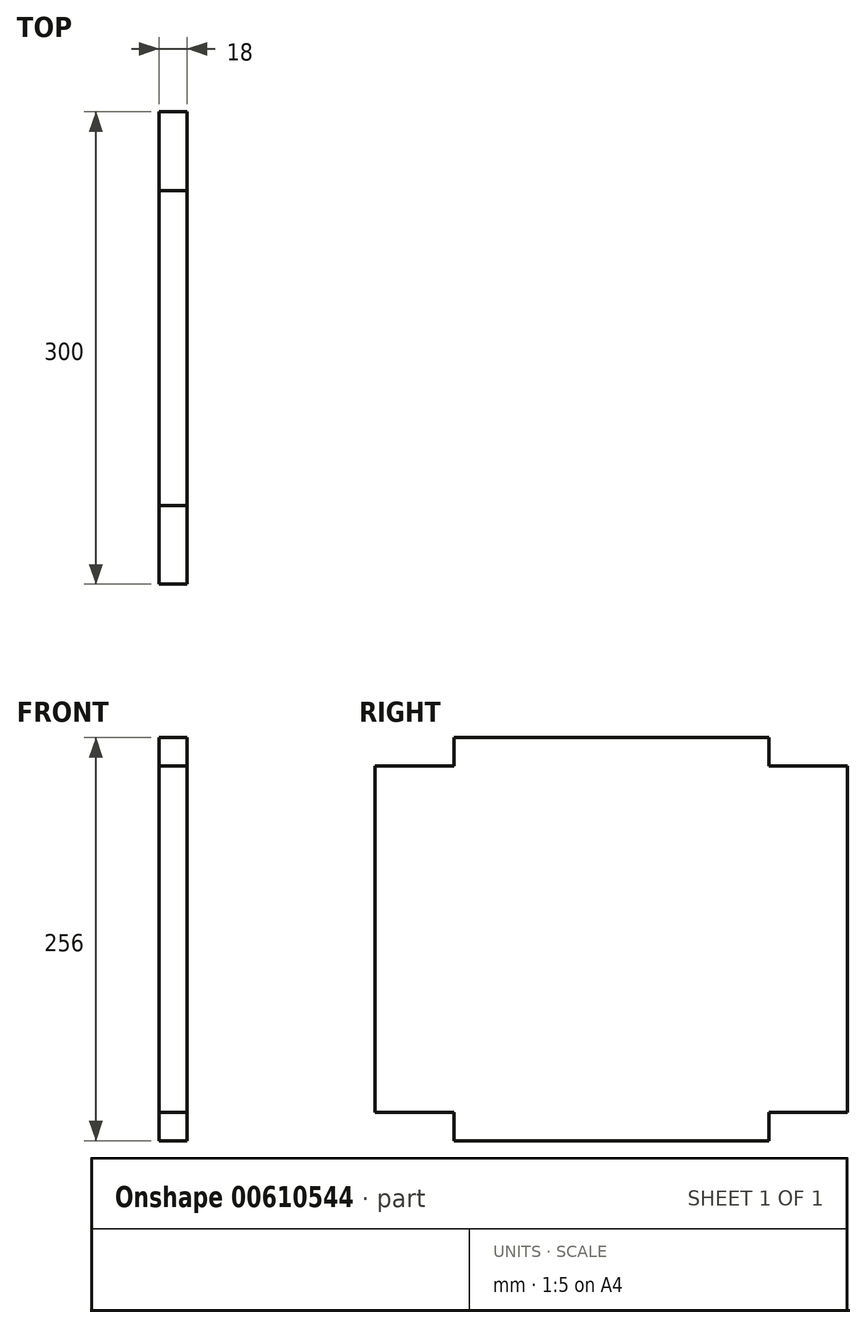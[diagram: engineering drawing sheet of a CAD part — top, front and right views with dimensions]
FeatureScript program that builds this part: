
annotation { "Feature Type Name" : "Feature", "Feature Type Description" : "" }
export const myFeature = defineFeature(function(context is Context, id is Id, definition is map)
    precondition{}
    {
        {
            var Q0;
            Q0=qCreatedBy(makeId("Right.planeOp"),FACE);
            var sketch = newSketch(context, id + "F0", { "sketchPlane" : qUnion([Q0])});
            skLineSegment(sketch, "E0.bottom", {"start": v(-50, 0) * mm, "end": v(-250, 0) * mm});
            skLineSegment(sketch, "E0.top", {"start": v(-50, 256) * mm, "end": v(-250, 256) * mm});
            skLineSegment(sketch, "E0.left", {"start": v(0, 18) * mm, "end": v(0, 238) * mm});
            skLineSegment(sketch, "E0.right", {"start": v(-300, 18) * mm, "end": v(-300, 238) * mm});
            skLineSegment(sketch, "E1.top", {"start": v(0, 238) * mm, "end": v(-50, 238) * mm});
            skLineSegment(sketch, "E1.right", {"start": v(-50, 256) * mm, "end": v(-50, 238) * mm});
            skLineSegment(sketch, "E2.top", {"start": v(-250, 238) * mm, "end": v(-300, 238) * mm});
            skLineSegment(sketch, "E2.left", {"start": v(-250, 256) * mm, "end": v(-250, 238) * mm});
            skLineSegment(sketch, "E3.bottom", {"start": v(-250, 18) * mm, "end": v(-300, 18) * mm});
            skLineSegment(sketch, "E3.left", {"start": v(-250, 18) * mm, "end": v(-250, 0) * mm});
            skLineSegment(sketch, "E4.bottom", {"start": v(0, 18) * mm, "end": v(-50, 18) * mm});
            skLineSegment(sketch, "E4.right", {"start": v(-50, 18) * mm, "end": v(-50, 0) * mm});
            skSolve(sketch);
        }
        {
            var Q0;
            Q0=makeQuery(id+"F0.imprint","IMPRINT",FACE,{"disambiguationData":[TD([[makeQuery(id+"F0.imprint","IMPRINT",EDGE,{"derivedFrom":sQuery(id+"F0.wireOp",EDGE,"E0.bottom")}),-1.0]])]});
            extrude(context, id + "F1", {"entities" : qUnion([Q0]), "depth" : 18 * mm, "offsetDistance" : 25 * mm});
        }
    });
